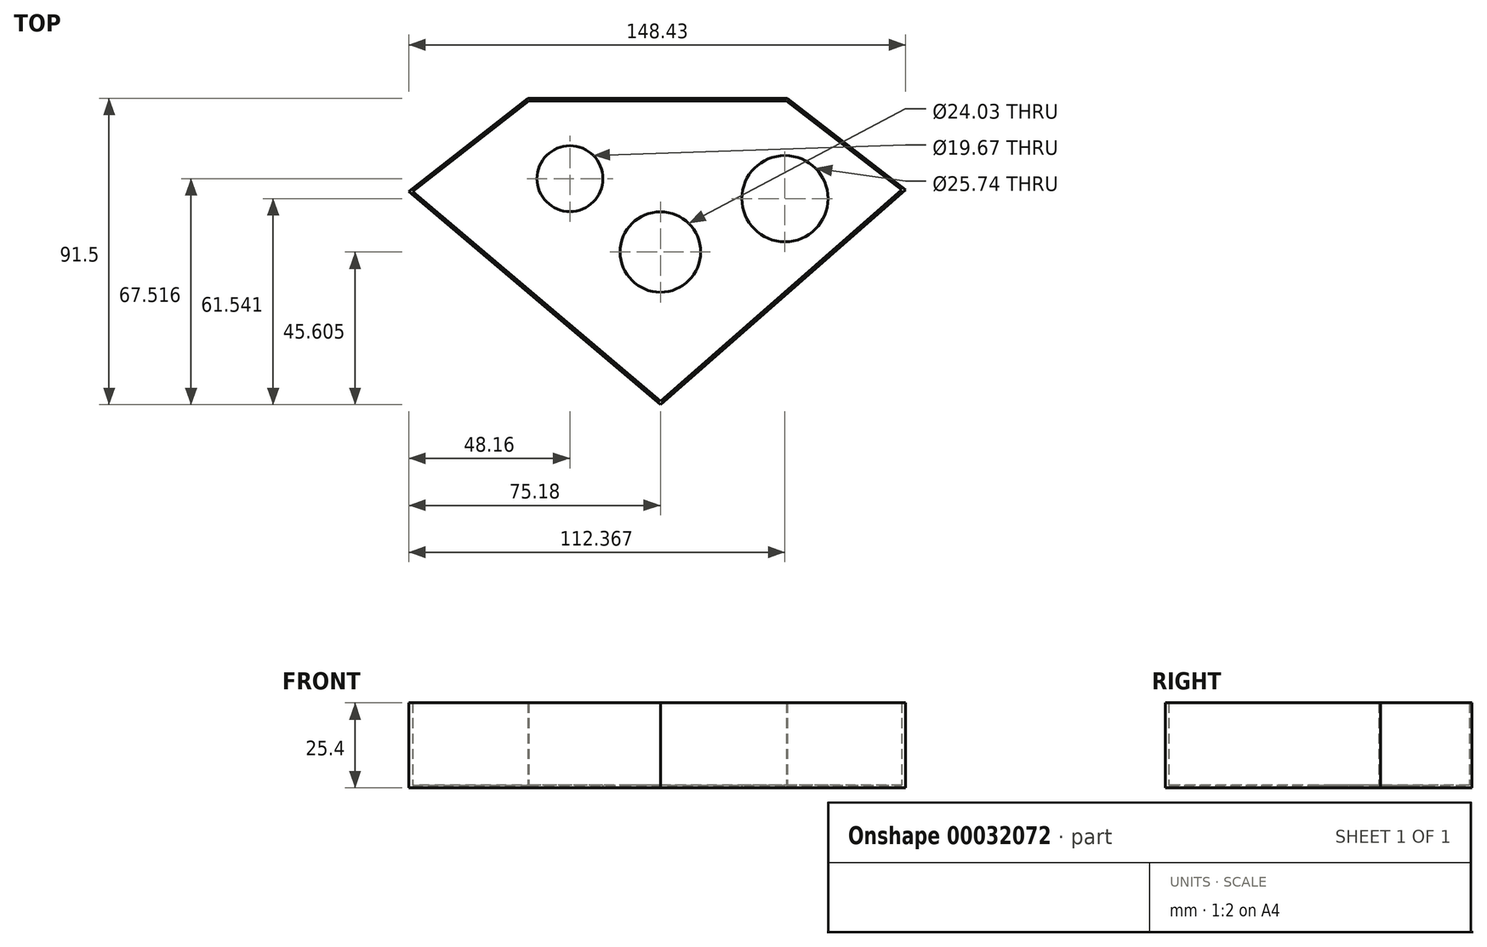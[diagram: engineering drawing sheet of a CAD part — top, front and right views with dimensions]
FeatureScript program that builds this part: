
annotation { "Feature Type Name" : "Feature", "Feature Type Description" : "" }
export const myFeature = defineFeature(function(context is Context, id is Id, definition is map)
    precondition{}
    {
        {
            var Q0;
            Q0=qCreatedBy(makeId("Top.planeOp"),FACE);
            var sketch = newSketch(context, id + "F0", { "sketchPlane" : qUnion([Q0])});
            skLineSegment(sketch, "E0", {"start": v(-39.61, 17.94) * mm, "end": v(37.93, 17.94) * mm});
            skLineSegment(sketch, "E1", {"start": v(37.93, 17.94) * mm, "end": v(73.25, -9.33) * mm});
            skLineSegment(sketch, "E2", {"start": v(73.25, -9.33) * mm, "end": v(0, -73.56) * mm});
            skLineSegment(sketch, "E3", {"start": v(0, -73.56) * mm, "end": v(-75.18, -9.85) * mm});
            skLineSegment(sketch, "E4", {"start": v(-75.18, -9.85) * mm, "end": v(-39.61, 17.94) * mm});
            skSolve(sketch);
        }
        {
            var Q0;
            Q0=makeQuery(id+"F0.imprint","IMPRINT",FACE,{"disambiguationData":[TD([[makeQuery(id+"F0.imprint","IMPRINT",EDGE,{"derivedFrom":sQuery(id+"F0.wireOp",EDGE,"E0")}),-1.0]])]});
            extrude(context, id + "F1", {"entities" : qUnion([Q0]), "depth" : 25.4 * mm});
        }
        {
            var Q0;
            Q0=makeQuery(id+"F1.opExtrude","CAP_FACE",FACE,{"disambiguationData":[OSD([sQuery(id+"F0.wireOp",EDGE,"E0"),sQuery(id+"F0.wireOp",EDGE,"E1"),sQuery(id+"F0.wireOp",EDGE,"E2"),sQuery(id+"F0.wireOp",EDGE,"E3"),sQuery(id+"F0.wireOp",EDGE,"E4")])],"isStart":false});
            shell(context, id + "F2", {"entities" : qUnion([Q0]), "thickness" : 0.76 * mm});
        }
        {
            var Q0;
            Q0=makeQuery(id+"F1.opExtrude","CAP_FACE",FACE,{"disambiguationData":[OSD([sQuery(id+"F0.wireOp",EDGE,"E0"),sQuery(id+"F0.wireOp",EDGE,"E1"),sQuery(id+"F0.wireOp",EDGE,"E2"),sQuery(id+"F0.wireOp",EDGE,"E3"),sQuery(id+"F0.wireOp",EDGE,"E4")])],"isStart":true});
            var sketch = newSketch(context, id + "F3", { "sketchPlane" : qUnion([Q0])});
            skCircle(sketch, "E5", {"center": v(0, 27.96) * mm, "radius": 12.01 * mm});
            skSolve(sketch);
        }
        {
            var Q0;
            Q0 = qSketchRegion(id + "F3", true);
            extrude(context, id + "F4", {"entities" : qUnion([Q0]), "operationType" : NewBodyOperationType.REMOVE, "oppositeDirection" : true, "depth" : 25.4 * mm});
        }
        {
            var Q0;
            Q0=makeQuery(id+"F1.opExtrude","CAP_FACE",FACE,{"disambiguationData":[OSD([sQuery(id+"F0.wireOp",EDGE,"E0"),sQuery(id+"F0.wireOp",EDGE,"E1"),sQuery(id+"F0.wireOp",EDGE,"E2"),sQuery(id+"F0.wireOp",EDGE,"E3"),sQuery(id+"F0.wireOp",EDGE,"E4")])],"isStart":true});
            var sketch = newSketch(context, id + "F5", { "sketchPlane" : qUnion([Q0])});
            skCircle(sketch, "E6", {"center": v(37.19, 12.02) * mm, "radius": 12.87 * mm});
            skCircle(sketch, "E7", {"center": v(-27.02, 6.04) * mm, "radius": 9.84 * mm});
            skSolve(sketch);
        }
        {
            var Q0;
            Q0 = qSketchRegion(id + "F5", true);
            extrude(context, id + "F6", {"entities" : qUnion([Q0]), "operationType" : NewBodyOperationType.REMOVE, "oppositeDirection" : true, "depth" : 25.4 * mm});
        }
    });
